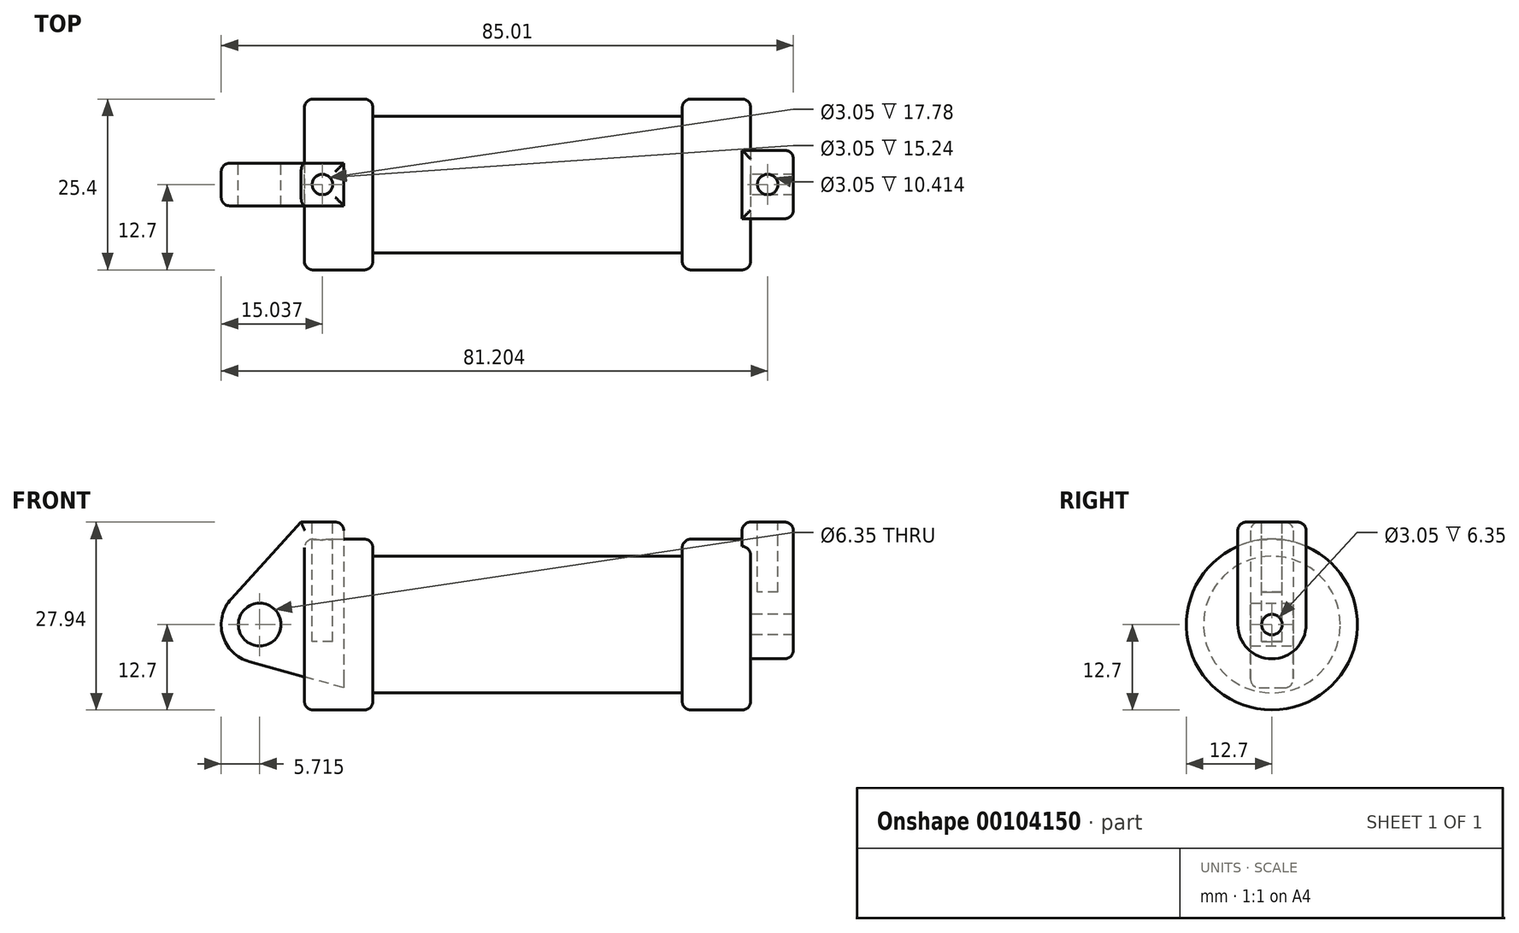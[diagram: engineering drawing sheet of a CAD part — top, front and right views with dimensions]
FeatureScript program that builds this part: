
annotation { "Feature Type Name" : "Feature", "Feature Type Description" : "" }
export const myFeature = defineFeature(function(context is Context, id is Id, definition is map)
    precondition{}
    {
        {
            var Q0;
            Q0=qCreatedBy(makeId("Front.planeOp"),FACE);
            var sketch = newSketch(context, id + "F0", { "sketchPlane" : qUnion([Q0])});
            skLineSegment(sketch, "E0", {"start": v(0, 0) * mm, "end": v(0, 12.7) * mm});
            skLineSegment(sketch, "E1", {"start": v(0, 12.7) * mm, "end": v(10.16, 12.7) * mm});
            skLineSegment(sketch, "E2", {"start": v(10.16, 12.7) * mm, "end": v(10.16, 10.16) * mm});
            skLineSegment(sketch, "E3", {"start": v(10.16, 10.16) * mm, "end": v(56.13, 10.16) * mm});
            skLineSegment(sketch, "E4", {"start": v(56.13, 10.16) * mm, "end": v(56.13, 12.7) * mm});
            skLineSegment(sketch, "E5", {"start": v(56.13, 12.7) * mm, "end": v(66.3, 12.7) * mm});
            skLineSegment(sketch, "E6", {"start": v(66.3, 12.7) * mm, "end": v(66.3, 0) * mm});
            skLineSegment(sketch, "E7", {"start": v(66.3, 0) * mm, "end": v(0, 0) * mm});
            skLineSegment(sketch, "E8", {"start": v(5.84, 15.24) * mm, "end": v(-0.5, 15.24) * mm});
            skLineSegment(sketch, "E9", {"start": v(-0.5, 15.24) * mm, "end": v(-10.88, 3.85) * mm});
            skLineSegment(sketch, "E10", {"start": v(0, 0) * mm, "end": v(-6.65, 0) * mm});
            skCircle(sketch, "E11", {"center": v(-6.65, 0) * mm, "radius": 5.72 * mm});
            skCircle(sketch, "E12", {"center": v(-6.65, 0) * mm, "radius": 3.18 * mm});
            skLineSegment(sketch, "E13", {"start": v(5.84, 15.24) * mm, "end": v(5.84, -9.4) * mm});
            skLineSegment(sketch, "E14", {"start": v(5.84, -9.4) * mm, "end": v(-8.18, -5.5) * mm});
            skSolve(sketch);
        }
        {
            var Q0;
            {var subQ0=sQuery(id+"F0.wireOp",EDGE,"E2");Q0=makeQuery(id+"F0.imprint","IMPRINT",FACE,{"disambiguationData":[TD([[makeQuery(id+"F0.imprint","IMPRINT",EDGE,{"derivedFrom":subQ0}),-1.0]])]});}
            var Q1;
            {var subQ0=sQuery(id+"F0.wireOp",EDGE,"E0");Q1=makeQuery(id+"F0.imprint","IMPRINT",FACE,{"disambiguationData":[TD([[makeQuery(id+"F0.imprint","IMPRINT",EDGE,{"derivedFrom":subQ0}),-1.0]])]});}
            var Q2;
            Q2=sQuery(id+"F0.wireOp",EDGE,"E7");
            revolve(context, id + "F1", {"entities" : qUnion([Q0, Q1]), "axis" : qUnion([Q2]), "revolveType" : RevolveType.FULL});
        }
        {
            var Q0;
            {var subQ3=sQuery(id+"F0.wireOp",EDGE,"E0");Q0=makeQuery(id+"F0.imprint","IMPRINT",FACE,{"disambiguationData":[TD([[makeQuery(id+"F0.imprint","IMPRINT",EDGE,{"derivedFrom":subQ3}),1.0]])]});}
            var Q1;
            {var subQ4=sQuery(id+"F0.wireOp",EDGE,"E12");Q1=makeQuery(id+"F0.imprint","IMPRINT",FACE,{"disambiguationData":[TD([[makeQuery(id+"F0.imprint","IMPRINT",EDGE,{"derivedFrom":subQ4}),-1.0]])]});}
            var Q2;
            {var subQ0=sQuery(id+"F0.wireOp",EDGE,"E14");Q2=makeQuery(id+"F0.imprint","IMPRINT",FACE,{"disambiguationData":[TD([[makeQuery(id+"F0.imprint","IMPRINT",EDGE,{"derivedFrom":subQ0}),-1.0]])]});}
            var Q3;
            {var subQ0=sQuery(id+"F0.wireOp",EDGE,"E0");Q3=makeQuery(id+"F0.imprint","IMPRINT",FACE,{"disambiguationData":[TD([[makeQuery(id+"F0.imprint","IMPRINT",EDGE,{"derivedFrom":subQ0}),-1.0]])]});}
            extrude(context, id + "F2", {"entities" : qUnion([Q0, Q1, Q2, Q3]), "depth" : 3.17 * mm, "hasSecondDirection" : true, "secondDirectionOppositeDirection" : true, "secondDirectionDepth" : 3.17 * mm});
        }
        {
            var Q0;
            Q0=makeQuery(id+"F1.opRevolve","SWEPT_FACE",FACE,{"disambiguationData":[OSD([sQuery(id+"F0.wireOp",EDGE,"E6")])]});
            var sketch = newSketch(context, id + "F3", { "sketchPlane" : qUnion([Q0])});
            skCircle(sketch, "E15", {"center": v(0, 0) * mm, "radius": 1.52 * mm});
            skCircle(sketch, "E16", {"center": v(0, 0) * mm, "radius": 5.08 * mm});
            skLineSegment(sketch, "E17", {"start": v(5.08, 0) * mm, "end": v(5.08, 15.24) * mm});
            skLineSegment(sketch, "E18", {"start": v(-5.08, 0) * mm, "end": v(-5.08, 15.24) * mm});
            skLineSegment(sketch, "E19", {"start": v(-5.08, 15.24) * mm, "end": v(5.08, 15.24) * mm});
            skSolve(sketch);
        }
        {
            var Q0;
            Q0 = qSketchRegion(id + "F3", true);
            extrude(context, id + "F4", {"entities" : qUnion([Q0]), "operationType" : NewBodyOperationType.ADD, "depth" : 6.35 * mm, "hasSecondDirection" : true, "secondDirectionOppositeDirection" : true, "secondDirectionDepth" : 1.27 * mm});
        }
        {
            var Q0;
            Q0=makeQuery(id+"F4.opExtrude","SWEPT_FACE",FACE,{"disambiguationData":[OSD([sQuery(id+"F3.wireOp",EDGE,"E19")])]});
            var sketch = newSketch(context, id + "F5", { "sketchPlane" : qUnion([Q0])});
            skCircle(sketch, "E20", {"center": v(68.83, 0) * mm, "radius": 1.52 * mm});
            skPoint(sketch, "E20.centerSnap0", {"position": v(65.02, 0) * mm});
            skPoint(sketch, "E20.centerSnap1", {"position": v(68.83, -5.08) * mm});
            skSolve(sketch);
        }
        {
            var Q0;
            Q0=makeQuery(id+"F2.opExtrude","SWEPT_FACE",FACE,{"disambiguationData":[OSD([sQuery(id+"F0.wireOp",EDGE,"E8")])]});
            var sketch = newSketch(context, id + "F6", { "sketchPlane" : qUnion([Q0])});
            skCircle(sketch, "E21", {"center": v(2.67, 0) * mm, "radius": 1.52 * mm});
            skPoint(sketch, "E21.centerSnap0", {"position": v(-0.5, 0) * mm});
            skPoint(sketch, "E21.centerSnap1", {"position": v(2.67, 3.18) * mm});
            skSolve(sketch);
        }
        {
            var Q0;
            Q0=makeQuery(id+"F6.imprint","IMPRINT",FACE,{"disambiguationData":[TD([[makeQuery(id+"F6.imprint","IMPRINT",EDGE,{"derivedFrom":sQuery(id+"F6.wireOp",EDGE,"E21")}),1.0]])]});
            extrude(context, id + "F7", {"entities" : qUnion([Q0]), "operationType" : NewBodyOperationType.REMOVE, "oppositeDirection" : true, "depth" : 17.78 * mm});
        }
        {
            var Q0;
            Q0=makeQuery(id+"F5.imprint","IMPRINT",FACE,{"disambiguationData":[TD([[makeQuery(id+"F5.imprint","IMPRINT",EDGE,{"derivedFrom":sQuery(id+"F5.wireOp",EDGE,"E20")}),1.0]])]});
            extrude(context, id + "F8", {"entities" : qUnion([Q0]), "operationType" : NewBodyOperationType.REMOVE, "oppositeDirection" : true, "depth" : 10.4 * mm});
        }
        {
            var Q0;
            Q0=makeQuery(id+"F2.opExtrude","CAP_EDGE",EDGE,{"disambiguationData":[OSD([sQuery(id+"F0.wireOp",EDGE,"E9")])],"isStart":false});
            var Q1;
            Q1=makeQuery(id+"F2.opExtrude","CAP_EDGE",EDGE,{"disambiguationData":[OSD([sQuery(id+"F0.wireOp",EDGE,"E9")])],"isStart":true});
            var Q2;
            Q2=makeQuery(id+"F2.opExtrude","CAP_EDGE",EDGE,{"disambiguationData":[OSD([sQuery(id+"F0.wireOp",EDGE,"E11")])],"isStart":true});
            var Q3;
            Q3=makeQuery(id+"F2.opExtrude","CAP_EDGE",EDGE,{"disambiguationData":[OSD([sQuery(id+"F0.wireOp",EDGE,"E14")])],"isStart":false});
            var Q4;
            Q4=makeQuery(id+"F2.opExtrude","CAP_EDGE",EDGE,{"disambiguationData":[OSD([sQuery(id+"F0.wireOp",EDGE,"E11")])],"isStart":false});
            var Q5;
            Q5=makeQuery(id+"F2.opExtrude","CAP_EDGE",EDGE,{"disambiguationData":[OSD([sQuery(id+"F0.wireOp",EDGE,"E14")])],"isStart":true});
            var Q6;
            Q6=makeQuery(id+"F2.opExtrude","CAP_EDGE",EDGE,{"disambiguationData":[OSD([sQuery(id+"F0.wireOp",EDGE,"E8")])],"isStart":false});
            var Q7;
            Q7=makeQuery(id+"F2.opExtrude","CAP_EDGE",EDGE,{"disambiguationData":[OSD([sQuery(id+"F0.wireOp",EDGE,"E8")])],"isStart":true});
            var Q8;
            Q8=makeQuery(id+"F2.opExtrude","SWEPT_EDGE",EDGE,{"disambiguationData":[OSD([sQuery(id+"F0.wireOp",EDGE,"E8"),sQuery(id+"F0.wireOp",EDGE,"E13")])]});
            var Q9;
            Q9=makeQuery(id+"F1.opRevolve","SWEPT_EDGE",EDGE,{"disambiguationData":[OSD([sQuery(id+"F0.wireOp",EDGE,"E0"),sQuery(id+"F0.wireOp",EDGE,"E1")])]});
            var Q10;
            Q10=makeQuery(id+"F1.opRevolve","SWEPT_EDGE",EDGE,{"disambiguationData":[OSD([sQuery(id+"F0.wireOp",EDGE,"E1"),sQuery(id+"F0.wireOp",EDGE,"E2")])]});
            fillet(context, id + "F9", {"entities" : qUnion([Q0, Q1, Q2, Q3, Q4, Q5, Q6, Q7, Q8, Q9, Q10]), "radius" : 1.27 * mm, "tangentPropagation" : true, "allowEdgeOverflow" : false});
        }
        {
            var Q0;
            Q0=makeQuery(id+"F4.opExtrude","CAP_EDGE",EDGE,{"disambiguationData":[OSD([sQuery(id+"F3.wireOp",EDGE,"E18")])],"isStart":false});
            var Q1;
            Q1=makeQuery(id+"F4.opExtrude","CAP_EDGE",EDGE,{"disambiguationData":[OSD([sQuery(id+"F3.wireOp",EDGE,"E16")])],"isStart":false});
            var Q2;
            Q2=makeQuery(id+"F4.opExtrude","CAP_EDGE",EDGE,{"disambiguationData":[OSD([sQuery(id+"F3.wireOp",EDGE,"E17")])],"isStart":false});
            var Q3;
            Q3=makeQuery(id+"F4.opExtrude","CAP_EDGE",EDGE,{"disambiguationData":[OSD([sQuery(id+"F3.wireOp",EDGE,"E19")])],"isStart":false});
            var Q4;
            Q4=makeQuery(id+"F4.opExtrude","CAP_EDGE",EDGE,{"disambiguationData":[OSD([sQuery(id+"F3.wireOp",EDGE,"E19")])],"isStart":true});
            var Q5;
            Q5=makeQuery(id+"F4.opExtrude","SWEPT_EDGE",EDGE,{"disambiguationData":[OSD([sQuery(id+"F3.wireOp",EDGE,"E18"),sQuery(id+"F3.wireOp",EDGE,"E19")])]});
            var Q6;
            Q6=makeQuery(id+"F4.opExtrude","SWEPT_EDGE",EDGE,{"disambiguationData":[OSD([sQuery(id+"F3.wireOp",EDGE,"E17"),sQuery(id+"F3.wireOp",EDGE,"E19")])]});
            var Q7;
            Q7=makeQuery(id+"F1.opRevolve","SWEPT_EDGE",EDGE,{"disambiguationData":[OSD([sQuery(id+"F0.wireOp",EDGE,"E5"),sQuery(id+"F0.wireOp",EDGE,"E6")])]});
            var Q8;
            Q8=makeQuery(id+"F1.opRevolve","SWEPT_EDGE",EDGE,{"disambiguationData":[OSD([sQuery(id+"F0.wireOp",EDGE,"E4"),sQuery(id+"F0.wireOp",EDGE,"E5")])]});
            fillet(context, id + "F10", {"entities" : qUnion([Q0, Q1, Q2, Q3, Q4, Q5, Q6, Q7, Q8]), "radius" : 1.27 * mm, "tangentPropagation" : true, "allowEdgeOverflow" : false});
        }
    });
